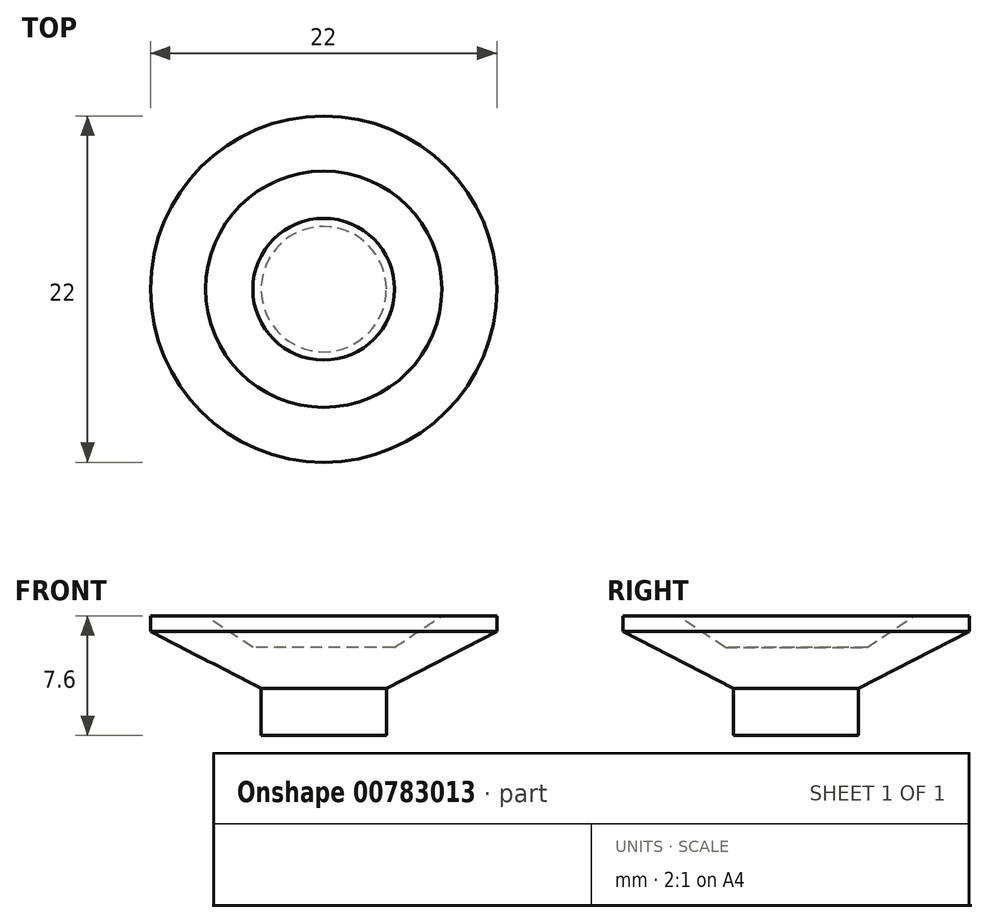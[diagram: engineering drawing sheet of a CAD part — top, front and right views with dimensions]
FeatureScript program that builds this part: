
annotation { "Feature Type Name" : "Feature", "Feature Type Description" : "" }
export const myFeature = defineFeature(function(context is Context, id is Id, definition is map)
    precondition{}
    {
        {
            var Q0;
            Q0=qCreatedBy(makeId("Front.planeOp"),FACE);
            var sketch = newSketch(context, id + "F0", { "sketchPlane" : qUnion([Q0])});
            skLineSegment(sketch, "E0", {"start": v(0, 0) * mm, "end": v(-3.98, 0) * mm});
            skLineSegment(sketch, "E1", {"start": v(-3.98, 0) * mm, "end": v(-3.98, 3) * mm});
            skLineSegment(sketch, "E2", {"start": v(-3.98, 3) * mm, "end": v(-11, 6.6) * mm});
            skLineSegment(sketch, "E3", {"start": v(0, 0) * mm, "end": v(0, 7.6) * mm});
            skLineSegment(sketch, "E4", {"start": v(-11, 6.6) * mm, "end": v(-11, 7.6) * mm});
            skLineSegment(sketch, "E5", {"start": v(-11, 7.6) * mm, "end": v(0, 7.6) * mm});
            skSolve(sketch);
        }
        {
            var Q0;
            Q0=qSketchRegion(id+"F0",true);
            var Q1;
            Q1=sQuery(id+"F0.wireOp",EDGE,"E3");
            revolve(context, id + "F1", {"surfaceOperationType" : NewSurfaceOperationType.NEW, "entities" : qUnion([Q0]), "axis" : qUnion([Q1]), "revolveType" : RevolveType.FULL});
        }
        {
            var Q0;
            Q0=makeQuery(id+"F1.opRevolve","SWEPT_FACE",FACE,{"disambiguationData":[OSD([sQuery(id+"F0.wireOp",EDGE,"E5")])]});
            var sketch = newSketch(context, id + "F2", { "sketchPlane" : qUnion([Q0])});
            skCircle(sketch, "E6", {"center": v(0, 0) * mm, "radius": 7.5 * mm});
            skSolve(sketch);
        }
        {
            var Q0;
            Q0=makeQuery(id+"F2.imprint","IMPRINT",FACE,{"disambiguationData":[TD([[makeQuery(id+"F2.imprint","IMPRINT",EDGE,{"derivedFrom":sQuery(id+"F2.wireOp",EDGE,"E6")}),1.0]])]});
            extrude(context, id + "F3", {"entities" : qUnion([Q0]), "operationType" : NewBodyOperationType.REMOVE, "oppositeDirection" : true, "depth" : 2 * mm, "offsetDistance" : 25 * mm});
        }
        {
            var Q0;
            Q0=makeQuery(id+"F3.boolean.opBoolean","COPY",EDGE,{"derivedFrom":makeQuery(id+"F3.opExtrude","CAP_EDGE",EDGE,{"disambiguationData":[OSD([sQuery(id+"F2.wireOp",EDGE,"E6")])],"isStart":false})});
            chamfer(context, id + "F4", {"entities" : qUnion([Q0]), "chamferType" : ChamferType.TWO_OFFSETS, "width1" : 3 * mm, "oppositeDirection" : false, "width2" : 2 * mm, "tangentPropagation" : true});
        }
    });
